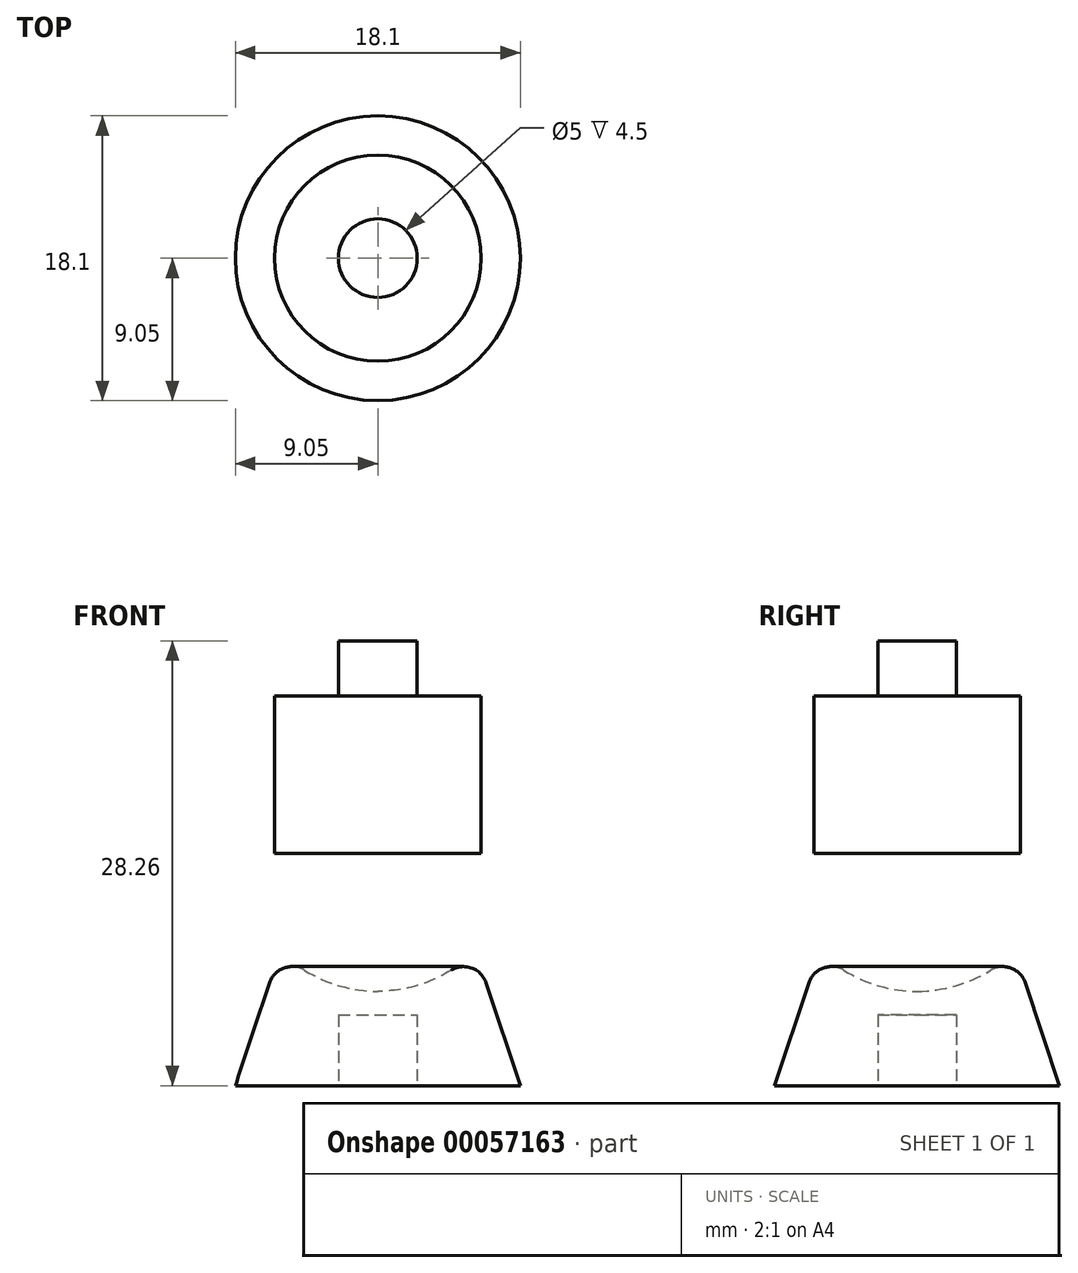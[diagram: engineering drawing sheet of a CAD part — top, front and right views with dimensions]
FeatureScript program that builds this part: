
annotation { "Feature Type Name" : "Feature", "Feature Type Description" : "" }
export const myFeature = defineFeature(function(context is Context, id is Id, definition is map)
    precondition{}
    {
        {
            var Q0;
            Q0=qCreatedBy(makeId("Front.planeOp"),FACE);
            var sketch = newSketch(context, id + "F0", { "sketchPlane" : qUnion([Q0])});
            skCircle(sketch, "E0", {"center": v(0, 0) * mm, "radius": 8.76 * mm, "construction": true});
            skLineSegment(sketch, "E1", {"start": v(0, -14.76) * mm, "end": v(9.05, -14.76) * mm});
            skLineSegment(sketch, "E2", {"start": v(0, -14.76) * mm, "end": v(0, -8.76) * mm});
            skLineSegment(sketch, "E3", {"start": v(0, 0) * mm, "end": v(6.2, -6.2) * mm, "construction": true});
            skLineSegment(sketch, "E4", {"start": v(6.2, -6.2) * mm, "end": v(9.05, -14.76) * mm});
            skArc(sketch, "E5", {"start": v(0, -8.76) * mm, "mid": v(3.35, -8.1) * mm, "end": v(6.2, -6.2) * mm});
            skSolve(sketch);
        }
        {
            var Q0;
            Q0 = qSketchRegion(id + "F0", true);
            var Q1;
            Q1=sQuery(id+"F0.wireOp",EDGE,"E2");
            revolve(context, id + "F1", {"entities" : qUnion([Q0]), "axis" : qUnion([Q1]), "revolveType" : RevolveType.FULL});
        }
        {
            var Q0;
            Q0=makeQuery(id+"F1.opRevolve","SWEPT_FACE",FACE,{"disambiguationData":[OSD([sQuery(id+"F0.wireOp",EDGE,"E1")])]});
            var sketch = newSketch(context, id + "F2", { "sketchPlane" : qUnion([Q0])});
            skCircle(sketch, "E6", {"center": v(0, 0) * mm, "radius": 2.5 * mm});
            skSolve(sketch);
        }
        {
            var Q0;
            Q0 = qSketchRegion(id + "F2", true);
            extrude(context, id + "F3", {"entities" : qUnion([Q0]), "operationType" : NewBodyOperationType.REMOVE, "oppositeDirection" : true, "depth" : 4.5 * mm});
        }
        {
            var Q0;
            Q0=makeQuery(id+"F1.opRevolve","SWEPT_EDGE",EDGE,{"disambiguationData":[OSD([sQuery(id+"F0.wireOp",EDGE,"E4"),sQuery(id+"F0.wireOp",EDGE,"E5")])]});
            fillet(context, id + "F4", {"entities" : qUnion([Q0]), "radius" : 1.5 * mm, "allowEdgeOverflow" : false});
        }
        {
            var Q0;
            Q0=qCreatedBy(makeId("Top.planeOp"),FACE);
            var sketch = newSketch(context, id + "F5", { "sketchPlane" : qUnion([Q0])});
            skCircle(sketch, "E7", {"center": v(0, 0) * mm, "radius": 6.55 * mm});
            skSolve(sketch);
        }
        {
            var Q0;
            Q0 = qSketchRegion(id + "F5", true);
            extrude(context, id + "F6", {"entities" : qUnion([Q0]), "depth" : 10 * mm});
        }
        {
            var Q0;
            Q0=makeQuery(id+"F6.opExtrude","CAP_FACE",FACE,{"disambiguationData":[OSD([sQuery(id+"F5.wireOp",EDGE,"E7")])],"isStart":false});
            var sketch = newSketch(context, id + "F7", { "sketchPlane" : qUnion([Q0])});
            skCircle(sketch, "E8.0", {"center": v(0, 0) * mm, "radius": 2.5 * mm});
            skSolve(sketch);
        }
        {
            var Q0;
            Q0 = qSketchRegion(id + "F7", true);
            extrude(context, id + "F8", {"entities" : qUnion([Q0]), "operationType" : NewBodyOperationType.ADD, "depth" : 3.5 * mm});
        }
    });
